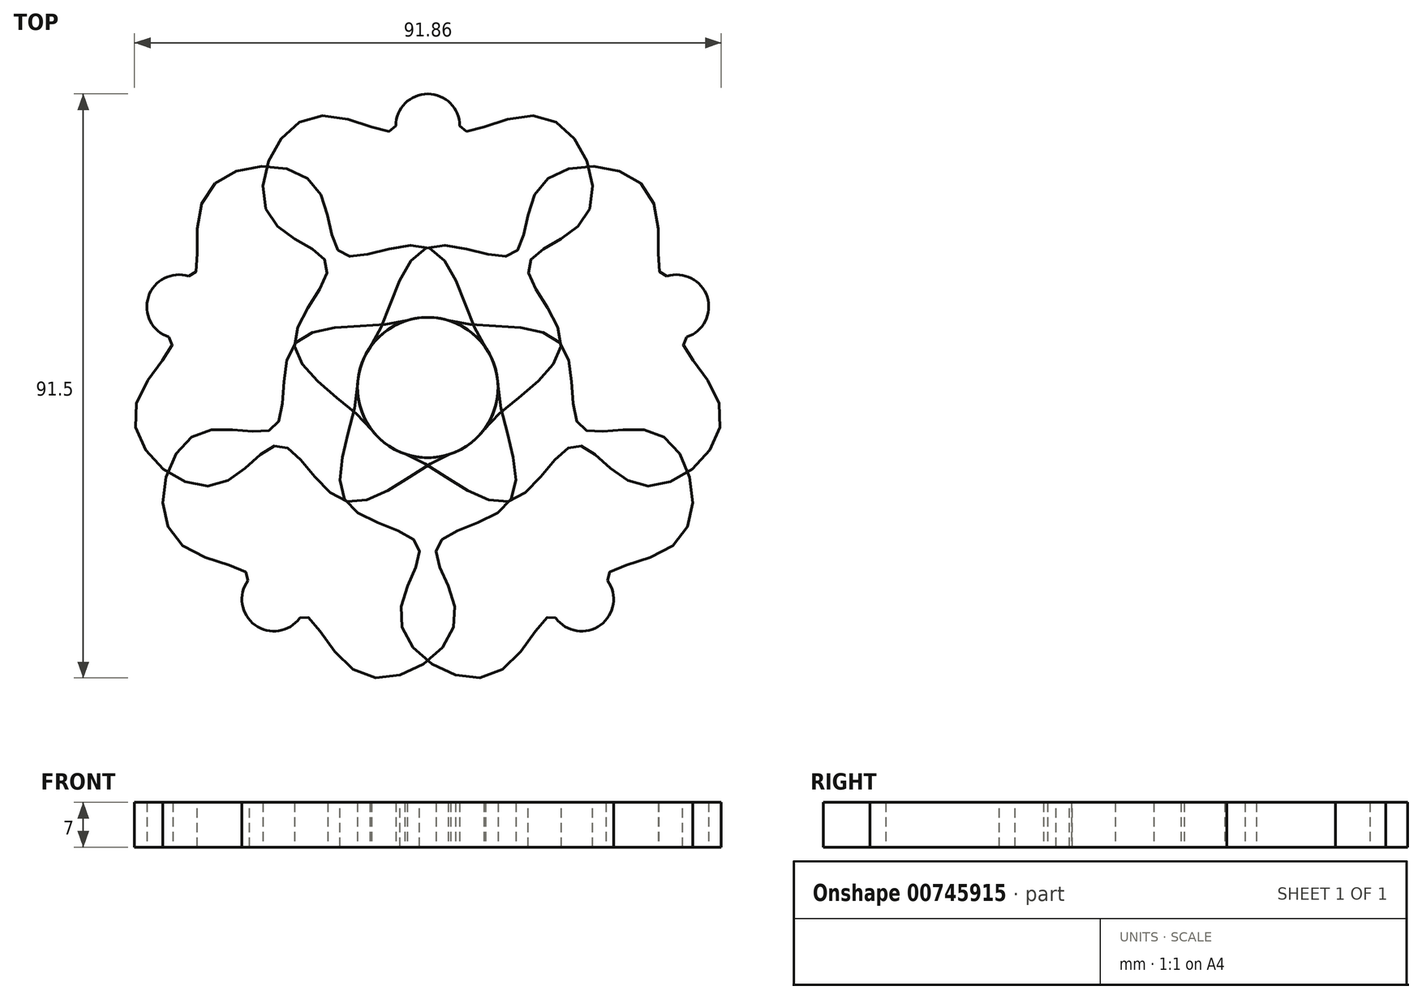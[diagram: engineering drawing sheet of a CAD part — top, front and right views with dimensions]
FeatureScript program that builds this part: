
annotation { "Feature Type Name" : "Feature", "Feature Type Description" : "" }
export const myFeature = defineFeature(function(context is Context, id is Id, definition is map)
    precondition{}
    {
        {
            var Q0;
            Q0=qCreatedBy(makeId("Top.planeOp"),FACE);
            var sketch = newSketch(context, id + "F0", { "sketchPlane" : qUnion([Q0])});
            skCircle(sketch, "E0", {"center": v(0, 0) * mm, "radius": 11 * mm});
            skLineSegment(sketch, "E1", {"start": v(0, 11) * mm, "end": v(0, 41) * mm});
            skCircle(sketch, "E2", {"center": v(0, 41) * mm, "radius": 5 * mm});
            skFitSpline(sketch, "E3", {"points": [v(5, 41) * mm, v(17.58, 42.5) * mm, v(25.04, 27.24) * mm, v(15.73, 19.12) * mm, v(20.9, 6.82) * mm, v(8.77, -6.64) * mm], "startDerivative": vector(0, -46.9) * mm, "endDerivative": vector(-44.7, -59.1) * mm});
            skFitSpline(sketch, "E4.MirrorCS", {"points": [v(-5, 41) * mm, v(-17.58, 42.5) * mm, v(-25.04, 27.24) * mm, v(-15.73, 19.12) * mm, v(-20.9, 6.82) * mm, v(-8.77, -6.64) * mm], "startDerivative": vector(0, -46.9) * mm, "endDerivative": vector(44.7, -59.1) * mm});
            skSolve(sketch);
        }
        {
            var Q0;
            {var subQ3=sQuery(id+"F0.wireOp",EDGE,"E4.MirrorCS");Q0=makeQuery(id+"F0.imprint","IMPRINT",FACE,{"disambiguationData":[TD([[makeQuery(id+"F0.imprint","IMPRINT",EDGE,{"derivedFrom":subQ3}),1.0]])]});}
            var Q1;
            {var subQ0=sQuery(id+"F0.wireOp",EDGE,"E2");var subQ1=makeQuery(id+"F0.imprint","INTERSECT",VERTEX,{"derivedFrom":[subQ0,sQuery(id+"F0.wireOp",EDGE,"E3")]});Q1=makeQuery(id+"F0.imprint","IMPRINT",FACE,{"disambiguationData":[TD([[makeQuery(id+"F0.imprint","IMPRINT",EDGE,{"disambiguationData":[TD([[subQ1,-1.0]])],"derivedFrom":subQ0}),1.0]])]});}
            var Q2;
            {var subQ3=sQuery(id+"F0.wireOp",EDGE,"E3");Q2=makeQuery(id+"F0.imprint","IMPRINT",FACE,{"disambiguationData":[TD([[makeQuery(id+"F0.imprint","IMPRINT",EDGE,{"derivedFrom":subQ3}),-1.0]])]});}
            extrude(context, id + "F1", {"entities" : qUnion([Q0, Q1, Q2]), "depth" : 7 * mm, "offsetDistance" : 25 * mm});
        }
        {
            var Q0;
            Q0=makeQuery(id+"F1.opExtrude","SWEPT_BODY",BODY,{"disambiguationData":[OSD([sQuery(id+"F0.wireOp",EDGE,"E0"),sQuery(id+"F0.wireOp",EDGE,"E2"),sQuery(id+"F0.wireOp",EDGE,"E3"),sQuery(id+"F0.wireOp",EDGE,"E4.MirrorCS")])]});
            var Q1;
            Q1=sQuery(id+"F0.wireOp",EDGE,"E0");
            circularPattern(context, id + "F2", {"entities" : qUnion([Q0]), "axis" : qUnion([Q1]), "angle" : 360 * degree, "instanceCount" : 5, "equalSpace" : true});
        }
    });
